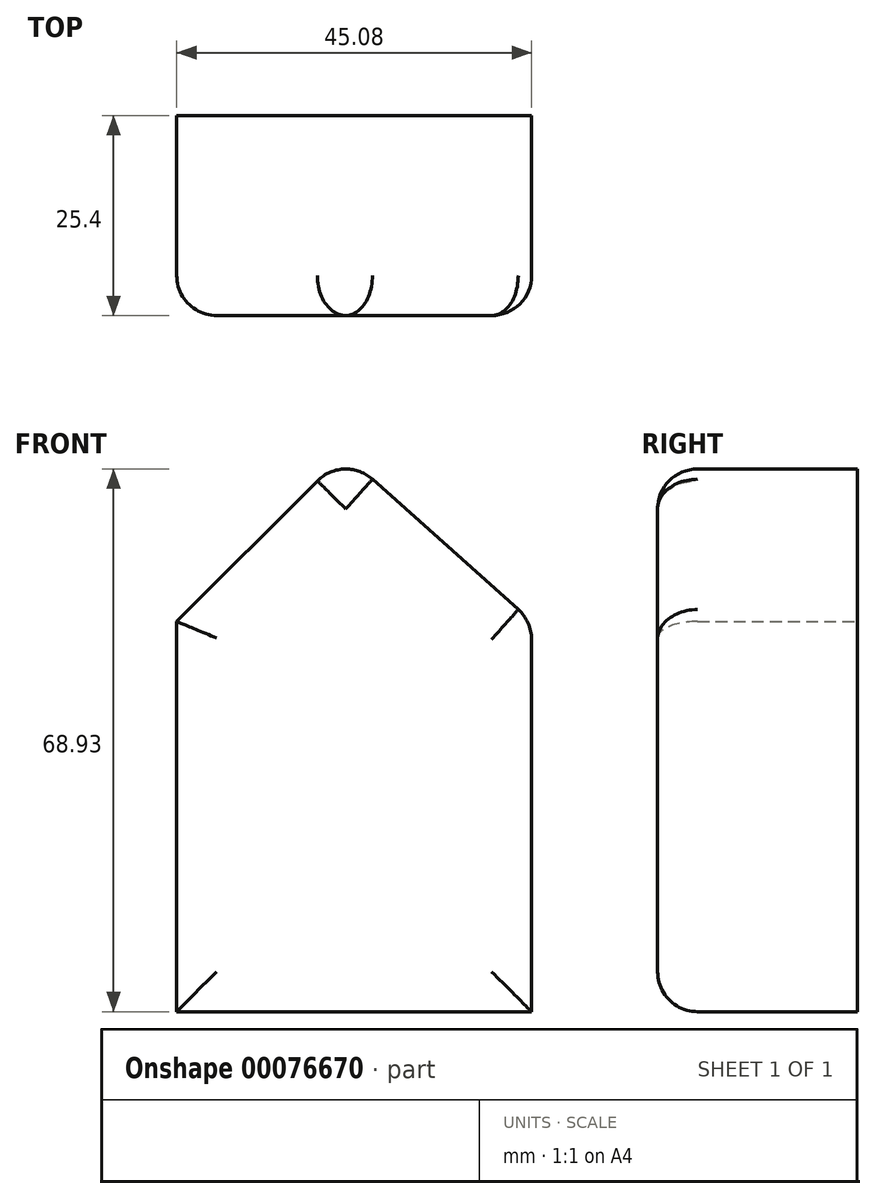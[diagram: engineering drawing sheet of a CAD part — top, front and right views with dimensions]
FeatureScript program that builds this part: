
annotation { "Feature Type Name" : "Feature", "Feature Type Description" : "" }
export const myFeature = defineFeature(function(context is Context, id is Id, definition is map)
    precondition{}
    {
        {
            var Q0;
            Q0=qCreatedBy(makeId("Front.planeOp"),FACE);
            var sketch = newSketch(context, id + "F0", { "sketchPlane" : qUnion([Q0])});
            skLineSegment(sketch, "E0", {"start": v(-26.54, -27.71) * mm, "end": v(-26.54, 21.86) * mm});
            skLineSegment(sketch, "E1", {"start": v(-26.54, 21.86) * mm, "end": v(18.54, 21.86) * mm});
            skLineSegment(sketch, "E2", {"start": v(-26.54, 21.86) * mm, "end": v(-5.27, 43.13) * mm});
            skLineSegment(sketch, "E3", {"start": v(-5.27, 43.13) * mm, "end": v(18.54, 21.86) * mm});
            skLineSegment(sketch, "E4", {"start": v(18.54, 21.86) * mm, "end": v(18.54, -32) * mm});
            skLineSegment(sketch, "E5", {"start": v(-26.54, -27.71) * mm, "end": v(18.54, -27.71) * mm});
            skLineSegment(sketch, "E6", {"start": v(18.54, -32) * mm, "end": v(18.54, -27.71) * mm});
            skSolve(sketch);
        }
        {
            var Q0;
            Q0 = qSketchRegion(id + "F0", true);
            extrude(context, id + "F1", {"entities" : qUnion([Q0]), "depth" : 25.4 * mm});
        }
        {
            var Q0;
            Q0=makeQuery(id+"F1.opExtrude","CAP_EDGE",EDGE,{"disambiguationData":[OSD([sQuery(id+"F0.wireOp",EDGE,"E3")])],"isStart":false});
            var Q1;
            Q1=makeQuery(id+"F1.opExtrude","SWEPT_EDGE",EDGE,{"disambiguationData":[OSD([sQuery(id+"F0.wireOp",EDGE,"E2"),sQuery(id+"F0.wireOp",EDGE,"E3")])]});
            fillet(context, id + "F2", {"entities" : qUnion([Q0, Q1]), "radius" : 5.08 * mm, "tangentPropagation" : true, "allowEdgeOverflow" : false});
        }
        {
            var Q0;
            Q0=makeQuery(id+"F1.opExtrude","CAP_EDGE",EDGE,{"disambiguationData":[OSD([sQuery(id+"F0.wireOp",EDGE,"E2")])],"isStart":false});
            var Q1;
            {var subQ0=sQuery(id+"F0.wireOp",EDGE,"E3");Q1=makeQuery(id+"F2.opFillet","BLEND_EDGE",EDGE,{"blendedFrom":[makeQuery(id+"F1.opExtrude","CAP_EDGE",EDGE,{"disambiguationData":[OSD([subQ0])],"isStart":false}),makeQuery(id+"F1.opExtrude","CAP_FACE",FACE,{"disambiguationData":[OSD([sQuery(id+"F0.wireOp",EDGE,"E0"),sQuery(id+"F0.wireOp",EDGE,"E2"),subQ0,sQuery(id+"F0.wireOp",EDGE,"E4"),sQuery(id+"F0.wireOp",EDGE,"E5")])],"isStart":false})],"blendedInto":[makeQuery(id+"F1.opExtrude","CAP_FACE",FACE,{"disambiguationData":[OSD([sQuery(id+"F0.wireOp",EDGE,"E0"),sQuery(id+"F0.wireOp",EDGE,"E2"),subQ0,sQuery(id+"F0.wireOp",EDGE,"E4"),sQuery(id+"F0.wireOp",EDGE,"E5")])],"isStart":false})]});}
            var Q2;
            Q2=makeQuery(id+"F1.opExtrude","CAP_FACE",FACE,{"disambiguationData":[OSD([sQuery(id+"F0.wireOp",EDGE,"E0"),sQuery(id+"F0.wireOp",EDGE,"E2"),sQuery(id+"F0.wireOp",EDGE,"E3"),sQuery(id+"F0.wireOp",EDGE,"E4"),sQuery(id+"F0.wireOp",EDGE,"E5")])],"isStart":false});
            var Q3;
            Q3=makeQuery(id+"F1.opExtrude","CAP_EDGE",EDGE,{"disambiguationData":[OSD([sQuery(id+"F0.wireOp",EDGE,"E0")])],"isStart":false});
            var Q4;
            Q4=makeQuery(id+"F1.opExtrude","CAP_EDGE",EDGE,{"disambiguationData":[OSD([sQuery(id+"F0.wireOp",EDGE,"E4")])],"isStart":false});
            var Q5;
            Q5=makeQuery(id+"F1.opExtrude","CAP_EDGE",EDGE,{"disambiguationData":[OSD([sQuery(id+"F0.wireOp",EDGE,"E5")])],"isStart":false});
            fillet(context, id + "F3", {"entities" : qUnion([Q0, Q1, Q2, Q3, Q4, Q5]), "radius" : 5.08 * mm, "tangentPropagation" : true, "allowEdgeOverflow" : false});
        }
    });
